# Revit family: Zumtobel IZURA
name_source: partatom
category: Lighting Fixtures
units: mm (PartAtom-declared; Revit-internal decimal feet)

## family parameters
Cut with Voids When Loaded = No
Host = Face
Light Source = No
Maintain Annotation Orientation = No
Part Type = Normal
Room Calculation Point = Yes
Round Connector Dimension = Use Diameter
Shared = No

## types (22) — shared parameters
Assembly Code = Pr_70_70_48_62
Description = Pendant Luminaire
Luminaire Height = 56 mm  [stored 0.183727 ft]
Luminaire Width = 56 mm  [stored 0.183727 ft]
Manufacturer = Zumtobel Lighting
SELECT GEARTRAY COLOR = SELECT GEARTRAY COLOR
SELECT HOUSING LENGTH = SELECT HOUSING LENGTH
SELECT HOUSING MATERIALS = SELECT HOUSING MATERIALS
SELECT PLASTIC SHADES COLOR = SELECT PLASTIC SHADES COLOR
SELECT SUSPENSION KIT COLOR = SELECT SUSPENSION KIT COLOR
URL = https://www.zumtobel.com
zero-valued in all types: Default Elevation

## per-type parameters (varying)
| type | Apparent Load | Geartray Black | Geartray White | Housing L12 | Housing L15 | Light Source Direct | Light Source Indirect | Luminaire Length | Material Housing Cover Inner | Material Housing Cover Outer | Model | Plastic Shades Black | Plastic Shades White | Power Factor | Suspension Kit Black | Suspension Kit Bronze | Suspension Kit Silver | Suspension Kit White | Type Image |
| IZU D/I 10k-935 L12 LDE BK GBKD HBKD | 69 VA | Yes | No | Yes | No | Zumtobel-Light Source-IZURA : 10k-935-DIR | Zumtobel-Light Source-IZURA : 10k-935-IND | 1233 mm  [stored 4.04528 ft] | Zumtobel-Aluminium-RAL 9005-Jet Black | Zumtobel-Aluminium-RAL 9005-Jet Black | 70515346 | Yes | No | 0.99 | Yes | No | No | No | IZURA-Black-Black.jpg |
| IZU D/I 10k-935 L12 LDE WH GWHD HWHD | 69 VA | No | Yes | Yes | No | Zumtobel-Light Source-IZURA : 10k-935-DIR | Zumtobel-Light Source-IZURA : 10k-935-IND | 1233 mm  [stored 4.04528 ft] | Zumtobel-Aluminium-RAL 9003-Signal White | Zumtobel-Aluminium-RAL 9003-Signal White | 70512803 | No | Yes | 0.99 | No | No | No | Yes | IZURA-White-White.jpg |
| IZU D/I 12k5-935 L15 LDE BK GBKD AIRT | 87 VA | Yes | No | No | Yes | Zumtobel-Light Source-IZURA : 12k5-935-DIR | Zumtobel-Light Source-IZURA : 12k5-935-IND | 1513 mm  [stored 4.96391 ft] | Zumtobel-Aluminium-RAL 3001-Signal Red | Zumtobel-Aluminium-RAL 9003-Signal White | 70515420 | Yes | No | 0.99 | No | No | No | Yes | IZURA-Airtrails.jpg |
| IZU D/I 12k5-935 L15 LDE BK GBKD CONC | 87 VA | Yes | No | No | Yes | Zumtobel-Light Source-IZURA : 12k5-935-DIR | Zumtobel-Light Source-IZURA : 12k5-935-IND | 1513 mm  [stored 4.96391 ft] | Zumtobel-Aluminium-RAL 9022-Pearl Dark Grey | Zumtobel-Aluminium-RAL 9022-Pearl Dark Grey | 70515422 | Yes | No | 0.99 | Yes | No | No | No | IZURA-Concrete.jpg |
| IZU D/I 12k5-935 L15 LDE BK GBKD HBKD | 87 VA | Yes | No | No | Yes | Zumtobel-Light Source-IZURA : 12k5-935-DIR | Zumtobel-Light Source-IZURA : 12k5-935-IND | 1513 mm  [stored 4.96391 ft] | Zumtobel-Aluminium-RAL 9005-Jet Black | Zumtobel-Aluminium-RAL 9005-Jet Black | 70515347 | Yes | No | 0.99 | Yes | No | No | No | IZURA-Black-Black.jpg |
| IZU D/I 12k5-935 L15 LDE BK GBKD RUST | 87 VA | Yes | No | No | Yes | Zumtobel-Light Source-IZURA : 12k5-935-DIR | Zumtobel-Light Source-IZURA : 12k5-935-IND | 1513 mm  [stored 4.96391 ft] | Zumtobel-Aluminium-RAL 9005-Jet Black | Zumtobel-Aluminium-RAL 8004-Copper Brown | 70515424 | Yes | No | 0.99 | Yes | No | No | No | IZURA-Rust.jpg |
| IZU D/I 12k5-935 L15 LDE BK GBKD SLTE | 87 VA | Yes | No | No | Yes | Zumtobel-Light Source-IZURA : 12k5-935-DIR | Zumtobel-Light Source-IZURA : 12k5-935-IND | 1513 mm  [stored 4.96391 ft] | Zumtobel-Aluminium-RAL 9005-Jet Black | Zumtobel-Aluminium-RAL 9011-Graphite Black | 70515425 | Yes | No | 0.99 | Yes | No | No | No | IZURA-Slate.jpg |
| IZU D/I 12k5-935 L15 LDE BK GWHD HWHD | 87 VA | No | Yes | No | Yes | Zumtobel-Light Source-IZURA : 12k5-935-DIR | Zumtobel-Light Source-IZURA : 12k5-935-IND | 1513 mm  [stored 4.96391 ft] | Zumtobel-Aluminium-RAL 9003-Signal White | Zumtobel-Aluminium-RAL 9003-Signal White | 70514018 | Yes | No | 0.99 | No | No | No | Yes | IZURA-White-Black.jpg |
| IZU D/I 12k5-935 L15 LDE WH GWHD 3DWH | 87 VA | No | Yes | No | Yes | Zumtobel-Light Source-IZURA : 12k5-935-DIR | Zumtobel-Light Source-IZURA : 12k5-935-IND | 1513 mm  [stored 4.96391 ft] | Zumtobel-Aluminium-RAL 9003-Signal White | Zumtobel-Aluminium-RAL 7035-Light Grey | 70515419 | No | Yes | 0.99 | No | No | No | Yes | IZURA-3D Ceramics.jpg |
| IZU D/I 12k5-935 L15 LDE WH GWHD E-AU | 87 VA | No | Yes | No | Yes | Zumtobel-Light Source-IZURA : 12k5-935-DIR | Zumtobel-Light Source-IZURA : 12k5-935-IND | 1513 mm  [stored 4.96391 ft] | Zumtobel-Aluminium-RAL 9003-Signal White | Zumtobel-Aluminium-RAL 1004-Golden Yellow | 70515353 | No | Yes | 0.99 | No | Yes | No | No | IZURA-Gold.jpg |
| IZU D/I 12k5-935 L15 LDE WH GWHD E-BZ | 87 VA | No | Yes | No | Yes | Zumtobel-Light Source-IZURA : 12k5-935-DIR | Zumtobel-Light Source-IZURA : 12k5-935-IND | 1513 mm  [stored 4.96391 ft] | Zumtobel-Aluminium-RAL 9003-Signal White | Zumtobel-Aluminium-RAL 1036-Pearl Gold | 70515354 | No | Yes | 0.99 | No | Yes | No | No | IZURA-Bronze.jpg |
| IZU D/I 12k5-935 L15 LDE WH GWHD E-SR | 87 VA | No | Yes | No | Yes | Zumtobel-Light Source-IZURA : 12k5-935-DIR | Zumtobel-Light Source-IZURA : 12k5-935-IND | 1513 mm  [stored 4.96391 ft] | Zumtobel-Aluminium-RAL 9003-Signal White | Zumtobel-Aluminium-RAL 7001-Silver Grey | 70515355 | No | Yes | 0.99 | No | No | Yes | No | IZURA-Inox.jpg |
| IZU D/I 12k5-935 L15 LDE WH GWHD HWHD | 87 VA | No | Yes | No | Yes | Zumtobel-Light Source-IZURA : 12k5-935-DIR | Zumtobel-Light Source-IZURA : 12k5-935-IND | 1513 mm  [stored 4.96391 ft] | Zumtobel-Aluminium-RAL 9003-Signal White | Zumtobel-Aluminium-RAL 9003-Signal White | 70515344 | No | Yes | 0.99 | No | No | No | Yes | IZURA-White-White.jpg |
| IZU D/I 12k5-935 L15 LDE WH GWHD MROC | 87 VA | No | Yes | No | Yes | Zumtobel-Light Source-IZURA : 12k5-935-DIR | Zumtobel-Light Source-IZURA : 12k5-935-IND | 1513 mm  [stored 4.96391 ft] | Zumtobel-Aluminium-RAL 1004-Golden Yellow | Zumtobel-Aluminium-RAL 9003-Signal White | 70515421 | No | Yes | 0.99 | No | No | No | Yes | IZURA-Marocco.jpg |
| IZU D/I 12k5-935 L15 LDE WH GWHD NUT | 87 VA | No | Yes | No | Yes | Zumtobel-Light Source-IZURA : 12k5-935-DIR | Zumtobel-Light Source-IZURA : 12k5-935-IND | 1513 mm  [stored 4.96391 ft] | Zumtobel-Aluminium-RAL 8011-Nut Brown | Zumtobel-Aluminium-RAL 8011-Nut Brown | 70515423 | No | Yes | 0.99 | No | Yes | No | No | IZURA-Wallnut.jpg |
| IZU D/I 12k5-935 L15 LDE WH GWHD OAK | 87 VA | No | Yes | No | Yes | Zumtobel-Light Source-IZURA : 12k5-935-DIR | Zumtobel-Light Source-IZURA : 12k5-935-IND | 1513 mm  [stored 4.96391 ft] | Zumtobel-Aluminium-RAL 9003-Signal White | Zumtobel-Aluminium-RAL 1002-Sand Yellow | 70515426 | No | Yes | 0.99 | No | No | No | Yes | IZURA-Oak.jpg |
| IZU D/I 12k5-935 L15 LDE WH GWHD WAVE | 87 VA | No | Yes | No | Yes | Zumtobel-Light Source-IZURA : 12k5-935-DIR | Zumtobel-Light Source-IZURA : 12k5-935-IND | 1513 mm  [stored 4.96391 ft] | Zumtobel-Aluminium-RAL 9003-Signal White | Zumtobel-Aluminium-RAL 9022-Pearl Dark Grey | 70515418 | No | Yes | 0.99 | No | No | No | Yes | IZURA-3D Waves.jpg |
| IZU DI 10k-935 L12 LDE BK GBKD HBKD | 65 VA | Yes | No | Yes | No | Zumtobel-Light Source-IZURA : 10k-935-DIR | Zumtobel-Light Source-IZURA : 10k-935-IND | 1233 mm  [stored 4.04528 ft] | Zumtobel-Aluminium-RAL 9005-Jet Black | Zumtobel-Aluminium-RAL 9005-Jet Black | 70515345 | Yes | No | 0.98 | Yes | No | No | No | IZURA-Black-Black.jpg |
| IZU DI 10k-935 L12 LDE WH GWHD HWHD | 65 VA | No | Yes | Yes | No | Zumtobel-Light Source-IZURA : 10k-935-DIR | Zumtobel-Light Source-IZURA : 10k-935-IND | 1233 mm  [stored 4.04528 ft] | Zumtobel-Aluminium-RAL 9003-Signal White | Zumtobel-Aluminium-RAL 9003-Signal White | 70512613 | No | Yes | 0.98 | No | No | No | Yes | IZURA-White-White.jpg |
| IZU DI 12k5-935 L15 LDE BK GBKD HBKD | 87 VA | Yes | No | No | Yes | Zumtobel-Light Source-IZURA : 12k5-935-DIR | Zumtobel-Light Source-IZURA : 12k5-935-IND | 1513 mm  [stored 4.96391 ft] | Zumtobel-Aluminium-RAL 9005-Jet Black | Zumtobel-Aluminium-RAL 9005-Jet Black | 70515180 | Yes | No | 0.99 | Yes | No | No | No | IZURA-Black-Black.jpg |
| IZU DI 12k5-935 L15 LDE BK GWHD HWHD | 87 VA | No | Yes | No | Yes | Zumtobel-Light Source-IZURA : 12k5-935-DIR | Zumtobel-Light Source-IZURA : 12k5-935-IND | 1513 mm  [stored 4.96391 ft] | Zumtobel-Aluminium-RAL 9003-Signal White | Zumtobel-Aluminium-RAL 9003-Signal White | 70512683 | Yes | No | 0.99 | No | No | No | Yes | IZURA-White-Black.jpg |
| IZU DI 12k5-935 L15 LDE WH GWHD HWHD | 87 VA | No | Yes | No | Yes | Zumtobel-Light Source-IZURA : 12k5-935-DIR | Zumtobel-Light Source-IZURA : 12k5-935-IND | 1513 mm  [stored 4.96391 ft] | Zumtobel-Aluminium-RAL 9003-Signal White | Zumtobel-Aluminium-RAL 9003-Signal White | 70515343 | No | Yes | 0.99 | No | No | No | Yes | IZURA-White-White.jpg |

note: [stored X ft] marks values corroborated as IEEE doubles in the binary element streams (Revit-internal decimal feet)

## geometry (parser evidence)
native form markers: Sweep x14
no freeform markers — native parametric forms only
